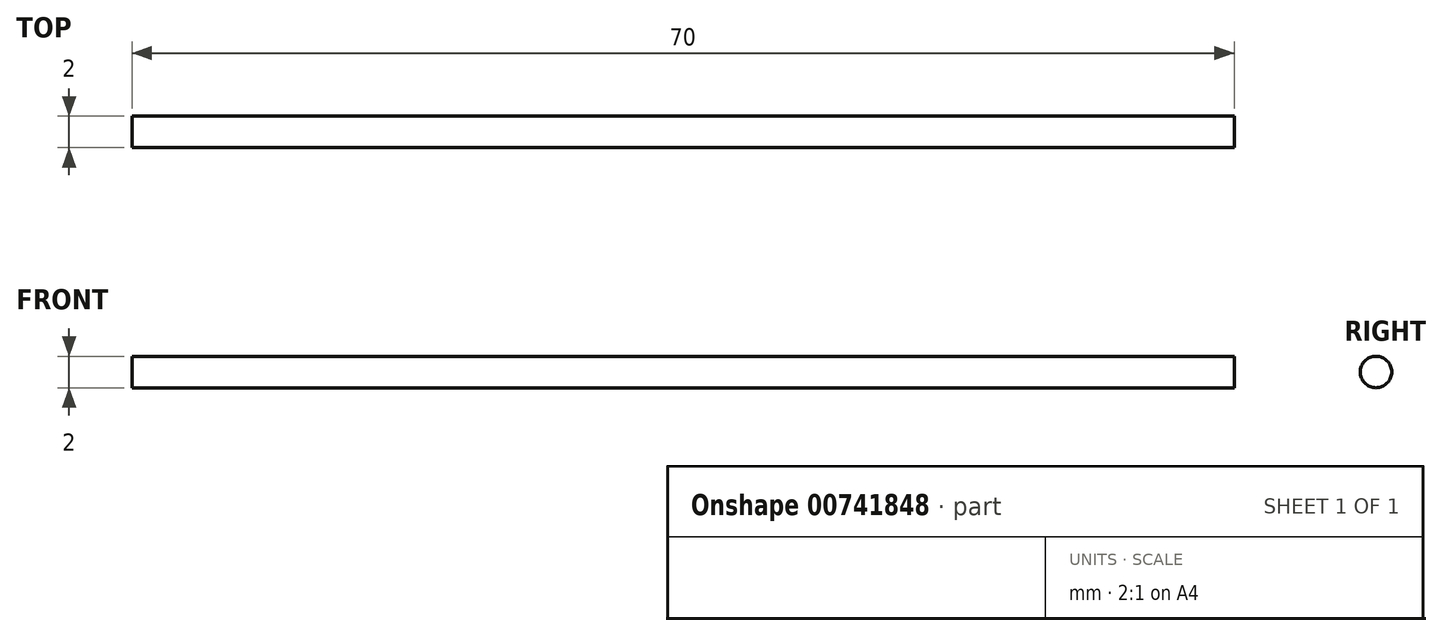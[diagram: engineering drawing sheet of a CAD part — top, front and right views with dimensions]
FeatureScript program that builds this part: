
annotation { "Feature Type Name" : "Feature", "Feature Type Description" : "" }
export const myFeature = defineFeature(function(context is Context, id is Id, definition is map)
    precondition{}
    {
        {
            var Q0;
            Q0=qCreatedBy(makeId("Top.planeOp"),FACE);
            var sketch = newSketch(context, id + "F0", { "sketchPlane" : qUnion([Q0])});
            skLineSegment(sketch, "E0.bottom", {"start": v(9.15, 15.7) * mm, "end": v(79.15, 15.7) * mm});
            skLineSegment(sketch, "E0.top", {"start": v(9.15, 14.7) * mm, "end": v(79.15, 14.7) * mm});
            skLineSegment(sketch, "E0.left", {"start": v(9.15, 15.7) * mm, "end": v(9.15, 14.7) * mm});
            skLineSegment(sketch, "E0.right", {"start": v(79.15, 15.7) * mm, "end": v(79.15, 14.7) * mm});
            skSolve(sketch);
        }
        {
            var Q0;
            Q0 = qSketchRegion(id + "F0", true);
            var Q1;
            Q1=sQuery(id+"F0.wireOp",EDGE,"E0.top");
            revolve(context, id + "F1", {"surfaceOperationType" : NewSurfaceOperationType.NEW, "entities" : qUnion([Q0]), "axis" : qUnion([Q1]), "revolveType" : RevolveType.FULL});
        }
    });
